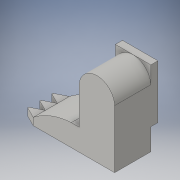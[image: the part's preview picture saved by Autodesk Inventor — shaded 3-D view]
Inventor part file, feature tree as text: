
AUTODESK INVENTOR PART (.ipt)
format: ipt  version: 2016 (Build 200138000, 138)  size: 203,776 bytes
history: native  units: in
note: dims shown in document units (in); Inventor stores cm internally (conversion verified against a paired STEP export)
features: extrude x9, sketch x9, reference x9, plane x1, fillet x1
ambient origin geometry x8: Origin, YZ Plane, XZ Plane, XY Plane, X Axis, Y Axis, Z Axis, Center Point
bodies: Solid1 (feature_tree)
feature tree (29):
  extrude  "Extrusion1"  Depth=0.0098in
  extrude  "Extrusion2"  Depth=0.0098in
  extrude  "Extrusion3"  Depth=0.1969in
  extrude  "Extrusion5"  Depth=0.6in
  extrude  "Extrusion6"  Depth=1.0in TaperAngle=0.0deg
  plane  "Work Plane1"
  extrude  "Extrusion7"  Depth=0.2in TaperAngle=0.0deg
  extrude  "Extrusion8"  [1 undecoded]
  extrude  "Extrusion9"  Depth=0.0394in
  extrude  "Extrusion10"  Depth=0.2362in TaperAngle=0.0deg
  fillet  "Fillet1"  Radius=0.5in
  sketch  "Sketch1"  dims[d0=0.0098in d1=0.0098in]
  reference  "Reference1"
  reference  "Reference2"
  reference  "Reference3"
  reference  "Reference4"
  reference  "Reference5"
  sketch  "Sketch2"  dims[d2=0.0098in d3=0.0098in]
  sketch  "Sketch3"  dims[d4=0.1969in d5=0.0in d6=0.98in]
  reference  "Reference6"
  sketch  "Sketch5"  dims[d7=1.0in d8=0.0in d9=0.6in]
  sketch  "Sketch6"  dims[d10=2.25in d12=1.0in d13=0.0in]
  sketch  "Sketch7"  dims[d16=0.3333in d22=0.2in d23=0.0in]
  reference  "Reference7"
  sketch  "Sketch8"  dims[d24=100.0in d25=0.0in d26=-0.5in]
  reference  "Reference8"
  sketch  "Sketch9"  dims[d27=0.0394in d28=0.0394in]
  sketch  "Sketch10"  dims[d29=0.0394in d30=0.2362in d31=0.0in d32=0.5in d33=0.0in d34=0.1378in d35=0.1969in d36=0.1969in d37=0.1211in d38=0.1211in d39=0.1969in d40=0.0in d41=0.1969in d42=0.0in d43=0.0197in]
  reference  "Reference9"
note: 1 required parameter value undecoded (feature->parameter linkage not recoverable at this tier; creation-order binding heuristic only, values carry confidence <= 0.55)
